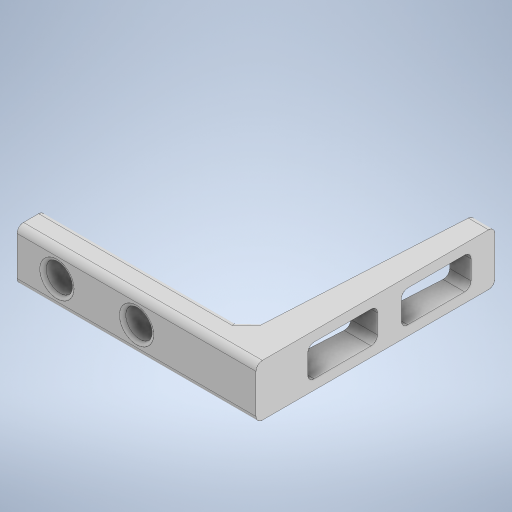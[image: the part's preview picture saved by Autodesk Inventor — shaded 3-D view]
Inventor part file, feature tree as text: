
AUTODESK INVENTOR PART (.ipt)
format: ipt  version: 2024.2 (Build 282272000, 272)  size: 326,656 bytes
history: native  units: mm
features: extrude x3, sketch x3, fillet x2, projected_geometry x2, other x1, chamfer x1
ambient origin geometry x8: Origin, YZ Plane, XZ Plane, XY Plane, X Axis, Y Axis, Z Axis, Center Point
bodies: Body1 (feature_tree)
feature tree (12):
  other  "Bryła1"
  extrude  "Wyciągnięcie proste1"  Depth=30.0mm
  extrude  "Wyciągnięcie proste2"  Depth=30.0mm
  extrude  "Wyciągnięcie proste3"  Depth=3.5mm
  chamfer  "Faza1"  Distance=2.5mm
  fillet  "Zaokrąglenie1"  Radius=4.0mm
  fillet  "Zaokrąglenie2"  Radius=6.5mm
  sketch  "Szkic1"
  sketch  "Szkic2"
  projected_geometry  "Pętla rzutowana1"
  sketch  "Szkic3"
  projected_geometry  "Pętla rzutowana2"
